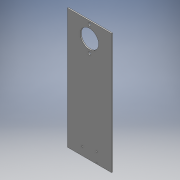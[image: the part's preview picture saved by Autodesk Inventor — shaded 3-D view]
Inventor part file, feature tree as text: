
AUTODESK INVENTOR PART (.ipt)
format: ipt  version: 2016 (Build 200138000, 138)  size: 119,808 bytes
history: native  units: mm
features: extrude x2, sketch x2, other x1
ambient origin geometry x8: Origin, YZ Plane, XZ Plane, XY Plane, X Axis, Y Axis, Z Axis, Center Point
bodies: Body1 (feature_tree)
feature tree (5):
  other  "ソリッド1"
  extrude  "押し出し1"  Depth=84.0mm
  extrude  "押し出し5"  Depth=230.0mm
  sketch  "スケッチ1"
  sketch  "スケッチ2"
